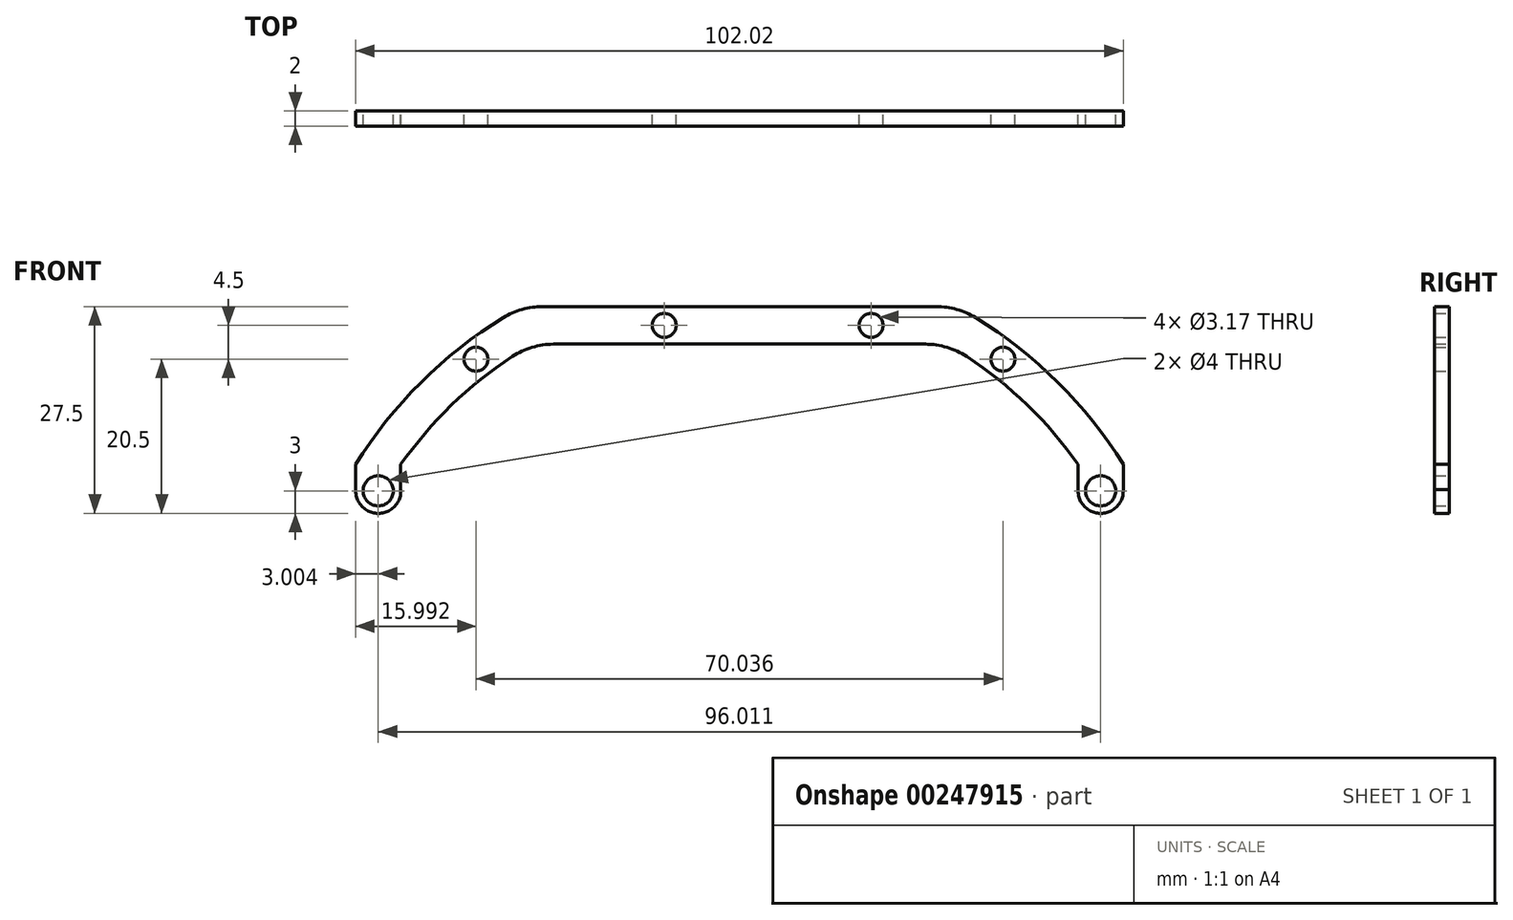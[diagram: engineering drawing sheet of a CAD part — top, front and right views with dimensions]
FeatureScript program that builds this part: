
annotation { "Feature Type Name" : "Feature", "Feature Type Description" : "" }
export const myFeature = defineFeature(function(context is Context, id is Id, definition is map)
    precondition{}
    {
        {
            var Q0;
            Q0=qCreatedBy(makeId("Front.planeOp"),FACE);
            var sketch = newSketch(context, id + "F0", { "sketchPlane" : qUnion([Q0])});
            skLineSegment(sketch, "E0", {"start": v(0, 0) * mm, "end": v(-45.01, 0) * mm, "construction": true});
            skLineSegment(sketch, "E1.top", {"start": v(-51, -3.5) * mm, "end": v(-45.01, -3.5) * mm});
            skLineSegment(sketch, "E1.left", {"start": v(-51, 0) * mm, "end": v(-51, -3.5) * mm});
            skLineSegment(sketch, "E1.right", {"start": v(-45.01, 0) * mm, "end": v(-45.01, -3.5) * mm});
            skArc(sketch, "E2", {"start": v(-51, -3.32) * mm, "mid": v(-48, -6.5) * mm, "end": v(-45.01, -3.32) * mm});
            skCircle(sketch, "E3", {"center": v(-48, -3.5) * mm, "radius": 2 * mm});
            skCircle(sketch, "E4", {"center": v(-35.02, 14) * mm, "radius": 1.59 * mm});
            skLineSegment(sketch, "E5.0", {"start": v(-26.17, 21) * mm, "end": v(0, 21) * mm});
            skArc(sketch, "E6.trimOffspring", {"start": v(-31.4, 19.52) * mm, "mid": v(-42.34, 10.9) * mm, "end": v(-51, 0) * mm});
            skArc(sketch, "E7.trimOffspring", {"start": v(-26.17, 21) * mm, "mid": v(-28.88, 20.62) * mm, "end": v(-31.4, 19.52) * mm});
            skArc(sketch, "E8.trimOffspring", {"start": v(-30.2, 14.36) * mm, "mid": v(-38.29, 7.88) * mm, "end": v(-45.01, 0) * mm});
            skLineSegment(sketch, "E9.trimOffspring", {"start": v(-24.71, 16) * mm, "end": v(0, 16) * mm});
            skArc(sketch, "E10.trimOffspring", {"start": v(-24.71, 16) * mm, "mid": v(-27.58, 15.58) * mm, "end": v(-30.2, 14.36) * mm});
            skLineSegment(sketch, "E11", {"start": v(0, 0) * mm, "end": v(0, 33.47) * mm});
            skArc(sketch, "E12.trimOffspring", {"start": v(0, 25.9) * mm, "mid": v(-27.28, 19) * mm, "end": v(-48.03, 0) * mm, "construction": true});
            skLineSegment(sketch, "E13.MirrorCS", {"start": v(26.17, 21) * mm, "end": v(0, 21) * mm});
            skLineSegment(sketch, "E14.MirrorCS", {"start": v(24.71, 16) * mm, "end": v(0, 16) * mm});
            skArc(sketch, "E15.MirrorCS", {"start": v(24.71, 16) * mm, "mid": v(27.58, 15.58) * mm, "end": v(30.2, 14.36) * mm});
            skArc(sketch, "E16.MirrorCS", {"start": v(26.17, 21) * mm, "mid": v(28.88, 20.62) * mm, "end": v(31.4, 19.52) * mm});
            skArc(sketch, "E17.MirrorCS", {"start": v(31.4, 19.52) * mm, "mid": v(42.34, 10.9) * mm, "end": v(51, 0) * mm});
            skArc(sketch, "E18.MirrorCS", {"start": v(30.2, 14.36) * mm, "mid": v(38.29, 7.88) * mm, "end": v(45.01, 0) * mm});
            skCircle(sketch, "E19.MirrorC", {"center": v(35.02, 14) * mm, "radius": 1.59 * mm});
            skLineSegment(sketch, "E20.MirrorCS", {"start": v(45.01, 0) * mm, "end": v(45.01, -3.5) * mm});
            skLineSegment(sketch, "E21.MirrorCS", {"start": v(51, 0) * mm, "end": v(51, -3.5) * mm});
            skArc(sketch, "E22.MirrorCS", {"start": v(51, -3.32) * mm, "mid": v(48, -6.5) * mm, "end": v(45.01, -3.32) * mm});
            skCircle(sketch, "E23.MirrorC", {"center": v(48, -3.5) * mm, "radius": 2 * mm});
            skCircle(sketch, "E24", {"center": v(-10, 18.5) * mm, "radius": 1.59 * mm});
            skCircle(sketch, "E25", {"center": v(17.5, 18.5) * mm, "radius": 1.59 * mm});
            skSolve(sketch);
        }
        {
            var Q0;
            Q0 = qSketchRegion(id + "F0", true);
            extrude(context, id + "F1", {"entities" : qUnion([Q0]), "depth" : 2 * mm});
        }
    });
